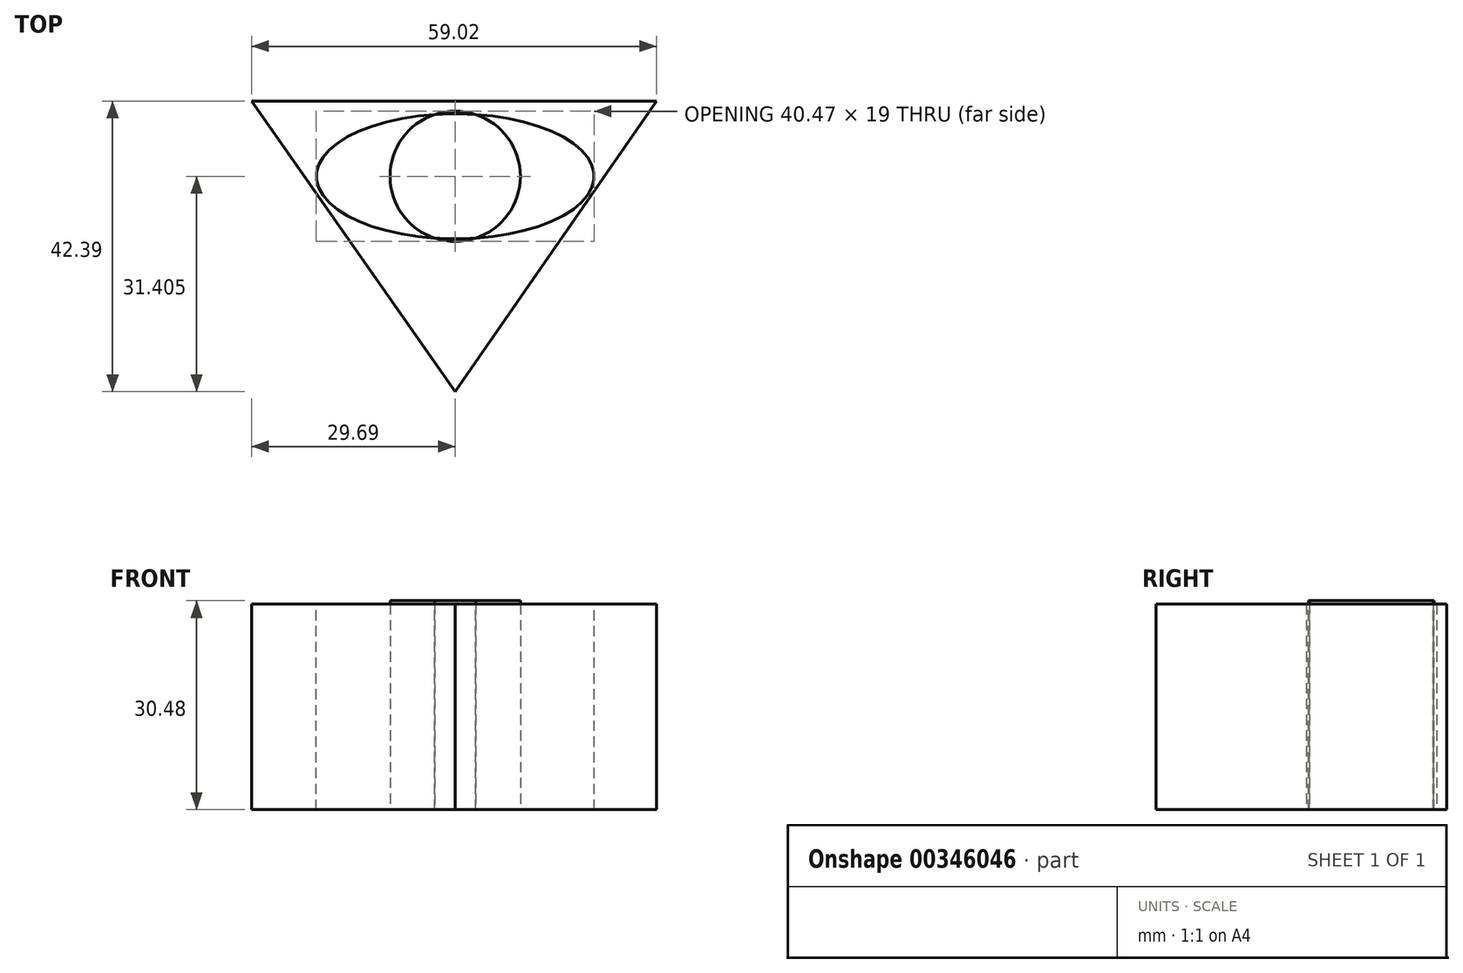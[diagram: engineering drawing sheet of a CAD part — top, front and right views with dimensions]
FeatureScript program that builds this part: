
annotation { "Feature Type Name" : "Feature", "Feature Type Description" : "" }
export const myFeature = defineFeature(function(context is Context, id is Id, definition is map)
    precondition{}
    {
        {
            var Q0;
            Q0=qCreatedBy(makeId("Top.planeOp"),FACE);
            var sketch = newSketch(context, id + "F0", { "sketchPlane" : qUnion([Q0])});
            skLineSegment(sketch, "E0", {"start": v(29.33, 0) * mm, "end": v(0, -42.39) * mm});
            skLineSegment(sketch, "E1", {"start": v(0, -42.39) * mm, "end": v(-29.69, 0) * mm});
            skLineSegment(sketch, "E2", {"start": v(29.33, 0) * mm, "end": v(-29.69, 0) * mm});
            skEllipse(sketch, "E3", {"center": v(0, -10.99) * mm, "majorRadius": 20.24 * mm, "minorRadius": 9.12 * mm, "majorAxis": v(-1, 0)});
            skCircle(sketch, "E4", {"center": v(0, -10.99) * mm, "radius": 9.5 * mm});
            skSolve(sketch);
        }
        {
            var Q0;
            Q0 = qSketchRegion(id + "F0", true);
            extrude(context, id + "F1", {"entities" : qUnion([Q0]), "depth" : 29.97 * mm});
        }
        {
            var Q0;
            Q0=makeQuery(id+"F0.imprint","IMPRINT",FACE,{"disambiguationData":[TD([[makeQuery(id+"F0.imprint","IMPRINT",EDGE,{"derivedFrom":sQuery(id+"F0.wireOp",EDGE,"E3")}),1.0]])]});
            extrude(context, id + "F2", {"entities" : qUnion([Q0]), "operationType" : NewBodyOperationType.ADD, "depth" : 30.48 * mm});
        }
    });
